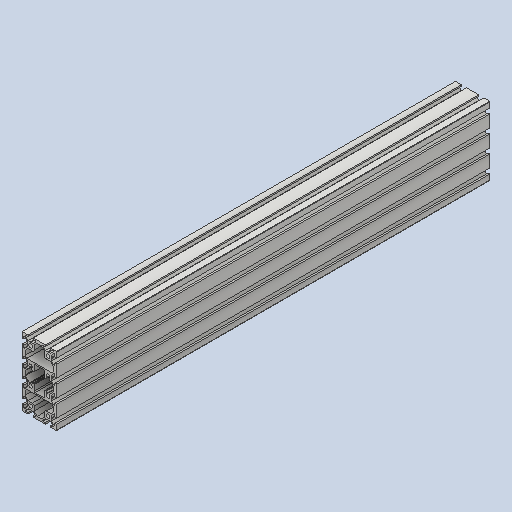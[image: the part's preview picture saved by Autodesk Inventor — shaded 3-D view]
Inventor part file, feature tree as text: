
AUTODESK INVENTOR PART (.ipt)
format: ipt  version: 2024 (Build 280153000, 153)  size: 749,568 bytes
history: native  units: mm
features: thread x16, sketch x2, extrude x1, hole x1, pattern_linear x1
ambient origin geometry x8: Origin, YZ Plane, XZ Plane, XY Plane, X Axis, Y Axis, Z Axis, Center Point
bodies: Solid1 (feature_tree)
feature tree (21):
  extrude  "Extrusion1"  Depth=20.0mm
  hole  "Hole1"  [1 undecoded]
  pattern_linear  "Rectangular Pattern1"  Spacing1=10.0mm  [1 undecoded]
  thread  "Thread2"  [1 undecoded]
  thread  "Thread3"  [1 undecoded]
  thread  "Thread4"  [1 undecoded]
  thread  "Thread5"  [1 undecoded]
  thread  "Thread6"  [1 undecoded]
  thread  "Thread7"  [1 undecoded]
  thread  "Thread8"  [1 undecoded]
  thread  "Thread9"  [1 undecoded]
  thread  "Thread10"  [1 undecoded]
  thread  "Thread11"  [1 undecoded]
  thread  "Thread12"  [1 undecoded]
  thread  "Thread13"  [1 undecoded]
  thread  "Thread14"  [1 undecoded]
  thread  "Thread15"  [1 undecoded]
  thread  "Thread16"  [1 undecoded]
  thread  "Thread17"  [1 undecoded]
  sketch  "Sketch_118"  dims[d2=4.2mm d3=6.0mm d4=4.0mm d5=2.0mm d6=90.0deg d7=425.0mm d8=0.0mm d9=20.0mm d11=20.0mm d12=20.0mm d14=60.0mm d17=10.0mm d18=0.0mm d19=10.0mm d20=0.0mm d21=10.0mm d22=0.0mm d23=10.0mm d24=0.0mm d25=10.0mm d26=0.0mm d27=10.0mm d28=0.0mm d29=10.0mm d30=0.0mm d31=10.0mm d32=0.0mm d33=10.0mm d34=0.0mm d35=10.0mm d36=0.0mm d37=10.0mm d38=0.0mm d39=10.0mm d40=0.0mm d41=10.0mm d42=0.0mm d43=10.0mm d44=0.0mm d45=10.0mm d46=0.0mm d47=10.0mm d48=0.0mm]
  sketch  "Sketch2"  dims[d0=500.0mm d1=0.0mm]
note: 18 required parameter values undecoded (feature->parameter linkage not recoverable at this tier; creation-order binding heuristic only, values carry confidence <= 0.55)
